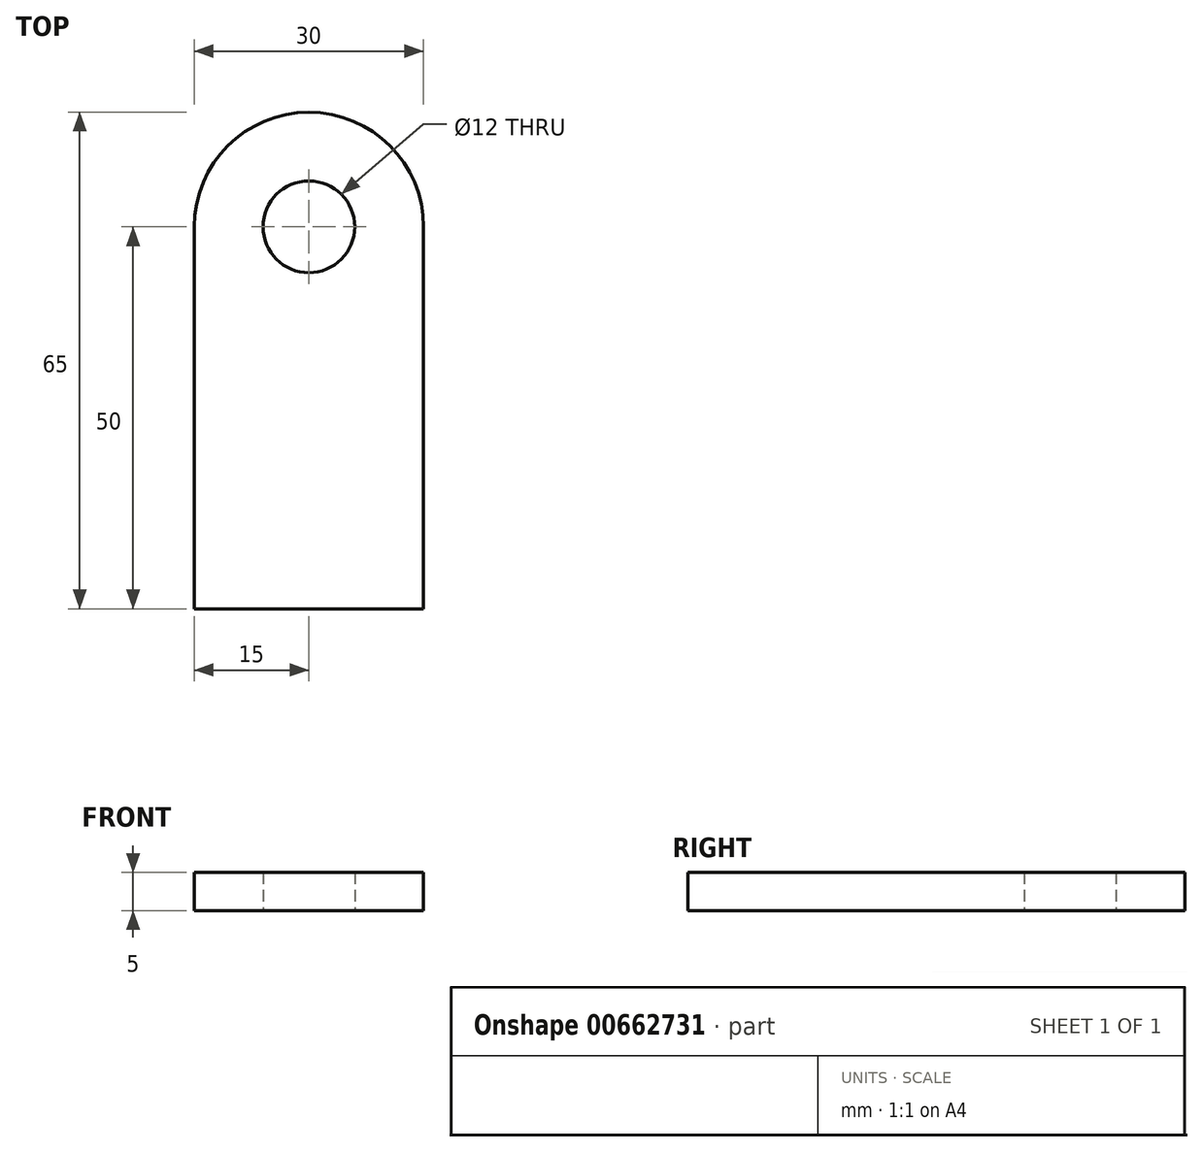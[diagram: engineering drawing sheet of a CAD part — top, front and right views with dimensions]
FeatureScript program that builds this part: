
annotation { "Feature Type Name" : "Feature", "Feature Type Description" : "" }
export const myFeature = defineFeature(function(context is Context, id is Id, definition is map)
    precondition{}
    {
        {
            var Q0;
            Q0=qCreatedBy(makeId("Top.planeOp"),FACE);
            var sketch = newSketch(context, id + "F0", { "sketchPlane" : qUnion([Q0])});
            skLineSegment(sketch, "E0", {"start": v(-15, 0) * mm, "end": v(-15, 50) * mm});
            skLineSegment(sketch, "E1", {"start": v(-15, 0) * mm, "end": v(15, 0) * mm});
            skLineSegment(sketch, "E2", {"start": v(15, 0) * mm, "end": v(15, 50) * mm});
            skArc(sketch, "E3", {"start": v(15, 50) * mm, "mid": v(0, 65) * mm, "end": v(-15, 50) * mm});
            skCircle(sketch, "E4", {"center": v(0, 50) * mm, "radius": 6 * mm});
            skSolve(sketch);
        }
        {
            var Q0;
            Q0=makeQuery(id+"F0.imprint","IMPRINT",FACE,{"disambiguationData":[TD([[makeQuery(id+"F0.imprint","IMPRINT",EDGE,{"derivedFrom":sQuery(id+"F0.wireOp",EDGE,"E0")}),-1.0]])]});
            extrude(context, id + "F1", {"entities" : qUnion([Q0]), "depth" : 5 * mm, "offsetDistance" : 25 * mm});
        }
    });
